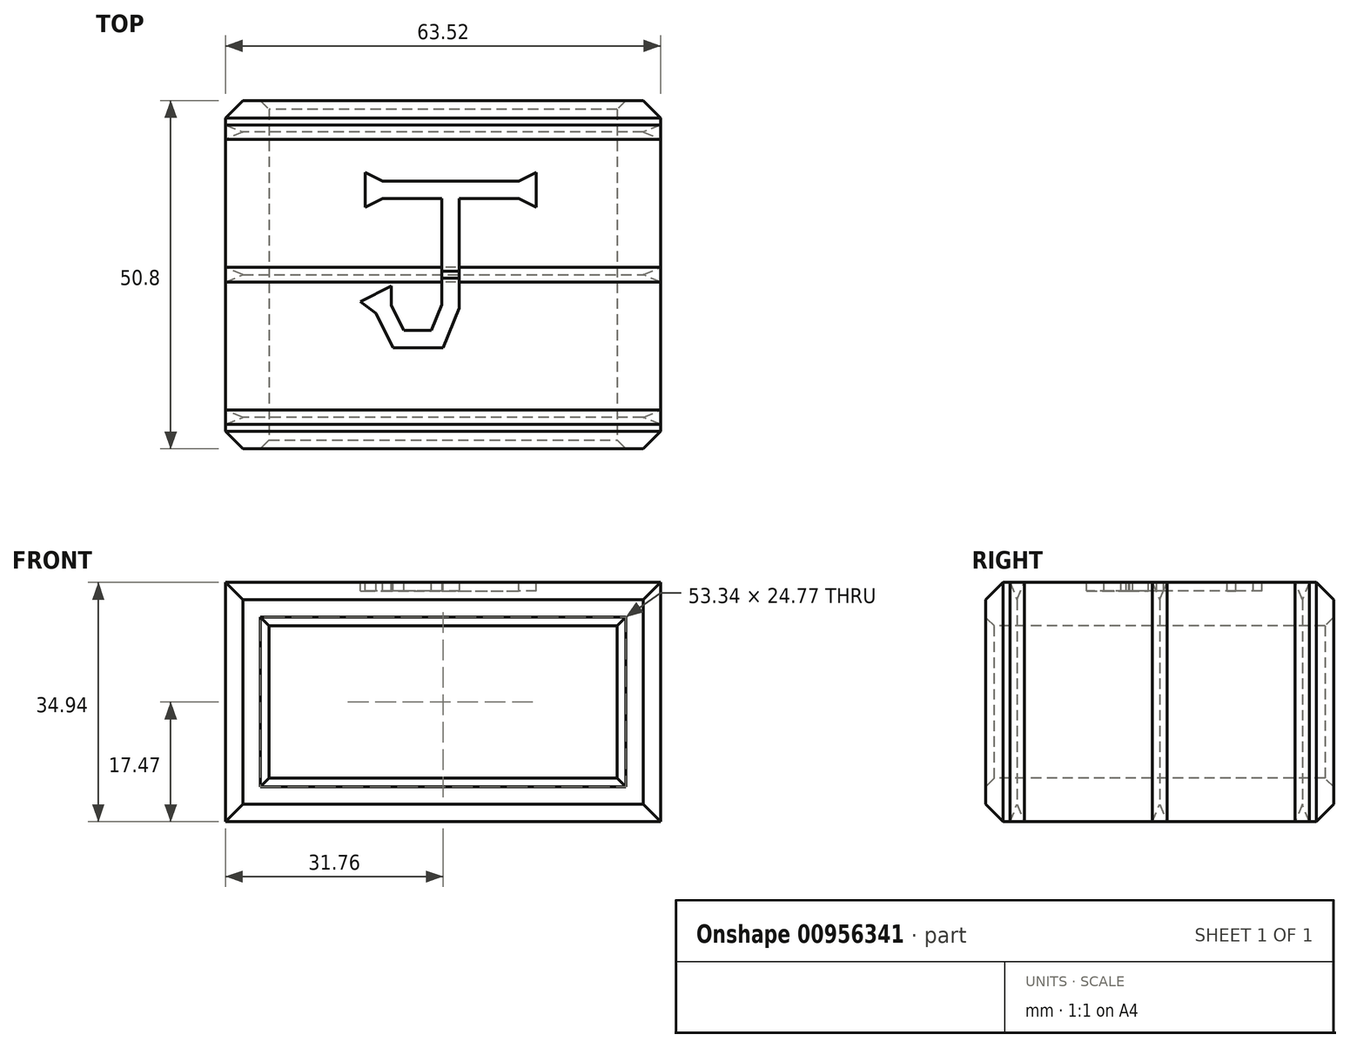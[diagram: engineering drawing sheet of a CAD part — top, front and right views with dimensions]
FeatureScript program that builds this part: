
annotation { "Feature Type Name" : "Feature", "Feature Type Description" : "" }
export const myFeature = defineFeature(function(context is Context, id is Id, definition is map)
    precondition{}
    {
        {
            var Q0;
            Q0=qCreatedBy(makeId("Front.planeOp"),FACE);
            var sketch = newSketch(context, id + "F0", { "sketchPlane" : qUnion([Q0])});
            skLineSegment(sketch, "E0.bottom", {"start": v(25.4, 11.11) * mm, "end": v(-25.4, 11.11) * mm});
            skLineSegment(sketch, "E0.top", {"start": v(25.4, -11.11) * mm, "end": v(-25.4, -11.11) * mm});
            skLineSegment(sketch, "E0.left", {"start": v(25.4, 11.11) * mm, "end": v(25.4, -11.11) * mm});
            skLineSegment(sketch, "E0.right", {"start": v(-25.4, 11.11) * mm, "end": v(-25.4, -11.11) * mm});
            skPoint(sketch, "E0.middle", {"position": v(0, 0) * mm});
            skLineSegment(sketch, "E1.0", {"start": v(30.48, 16.2) * mm, "end": v(-30.48, 16.2) * mm});
            skLineSegment(sketch, "E1.1", {"start": v(30.48, 16.2) * mm, "end": v(30.48, -16.2) * mm});
            skLineSegment(sketch, "E1.2", {"start": v(30.48, -16.2) * mm, "end": v(-30.48, -16.2) * mm});
            skLineSegment(sketch, "E1.3", {"start": v(-30.48, 16.2) * mm, "end": v(-30.48, -16.2) * mm});
            skSolve(sketch);
        }
        {
            var Q0;
            Q0=qCreatedBy(makeId("Right.planeOp"),FACE);
            var sketch = newSketch(context, id + "F1", { "sketchPlane" : qUnion([Q0])});
            skLineSegment(sketch, "E2", {"start": v(50.8, 11.11) * mm, "end": v(50.8, 14.92) * mm});
            skLineSegment(sketch, "E3", {"start": v(50.8, 14.92) * mm, "end": v(48.25, 17.47) * mm});
            skLineSegment(sketch, "E4", {"start": v(48.25, 17.47) * mm, "end": v(47.27, 17.47) * mm});
            skLineSegment(sketch, "E5", {"start": v(47.27, 17.47) * mm, "end": v(46.21, 14.92) * mm});
            skLineSegment(sketch, "E6", {"start": v(46.21, 14.92) * mm, "end": v(45.16, 17.47) * mm});
            skLineSegment(sketch, "E7", {"start": v(45.16, 17.47) * mm, "end": v(26.46, 17.47) * mm});
            skLineSegment(sketch, "E8", {"start": v(26.46, 17.47) * mm, "end": v(25.4, 14.92) * mm});
            skLineSegment(sketch, "E9", {"start": v(25.4, 14.92) * mm, "end": v(24.34, 17.47) * mm});
            skLineSegment(sketch, "E10", {"start": v(24.34, 17.47) * mm, "end": v(5.64, 17.47) * mm});
            skLineSegment(sketch, "E11", {"start": v(5.64, 17.47) * mm, "end": v(4.59, 14.92) * mm});
            skLineSegment(sketch, "E12", {"start": v(4.59, 14.92) * mm, "end": v(3.53, 17.47) * mm});
            skLineSegment(sketch, "E13", {"start": v(3.53, 17.47) * mm, "end": v(2.55, 17.47) * mm});
            skLineSegment(sketch, "E14", {"start": v(2.55, 17.47) * mm, "end": v(0, 14.92) * mm});
            skLineSegment(sketch, "E15", {"start": v(0, 14.92) * mm, "end": v(0, 11.11) * mm});
            skLineSegment(sketch, "E16", {"start": v(46.21, 14.92) * mm, "end": v(46.21, 38.18) * mm, "construction": true});
            skLineSegment(sketch, "E17", {"start": v(25.4, 14.92) * mm, "end": v(25.4, 36.3) * mm, "construction": true});
            skLineSegment(sketch, "E18", {"start": v(25.4, 36.3) * mm, "end": v(41.2, 36.3) * mm, "construction": true});
            skLineSegment(sketch, "E19", {"start": v(4.59, 14.92) * mm, "end": v(4.59, 35.3) * mm, "construction": true});
            skLineSegment(sketch, "E20", {"start": v(0, 14.92) * mm, "end": v(0, 38.69) * mm, "construction": true});
            skLineSegment(sketch, "E21", {"start": v(50.8, 14.92) * mm, "end": v(50.8, 38.2) * mm, "construction": true});
            skLineSegment(sketch, "E22", {"start": v(50.8, 14.92) * mm, "end": v(0, 14.92) * mm, "construction": true});
            skLineSegment(sketch, "E23", {"start": v(0, 11.11) * mm, "end": v(50.8, 11.11) * mm});
            skPoint(sketch, "E24.start.orphan", {"position": v(0, -70.86) * mm});
            skSolve(sketch);
        }
        {
            var Q0;
            Q0=makeQuery(id+"F1.imprint","IMPRINT",FACE,{"disambiguationData":[TD([[makeQuery(id+"F1.imprint","IMPRINT",EDGE,{"derivedFrom":sQuery(id+"F1.wireOp",EDGE,"E2")}),1.0]])]});
            var sketch = newSketch(context, id + "F2", { "sketchPlane" : qUnion([Q0])});
            skLineSegment(sketch, "E25", {"start": v(47.27, 17.47) * mm, "end": v(45.16, 17.47) * mm});
            skLineSegment(sketch, "E26", {"start": v(45.16, 17.47) * mm, "end": v(46.21, 14.92) * mm});
            skLineSegment(sketch, "E27", {"start": v(46.21, 14.92) * mm, "end": v(47.27, 17.47) * mm});
            skLineSegment(sketch, "E28", {"start": v(26.46, 17.47) * mm, "end": v(24.34, 17.47) * mm});
            skLineSegment(sketch, "E29", {"start": v(24.34, 17.47) * mm, "end": v(25.4, 14.92) * mm});
            skLineSegment(sketch, "E30", {"start": v(25.4, 14.92) * mm, "end": v(26.46, 17.47) * mm});
            skLineSegment(sketch, "E31", {"start": v(5.64, 17.47) * mm, "end": v(4.59, 14.92) * mm});
            skLineSegment(sketch, "E32", {"start": v(4.59, 14.92) * mm, "end": v(3.53, 17.47) * mm});
            skLineSegment(sketch, "E33", {"start": v(3.53, 17.47) * mm, "end": v(5.64, 17.47) * mm});
            skSolve(sketch);
        }
        {
            var Q0;
            Q0=makeQuery(id+"F1.imprint","IMPRINT",FACE,{"disambiguationData":[TD([[makeQuery(id+"F1.imprint","IMPRINT",EDGE,{"derivedFrom":sQuery(id+"F1.wireOp",EDGE,"E2")}),1.0]])]});
            var Q1;
            Q1=sQuery(id+"F0.wireOp",EDGE,"E0.bottom");
            var Q2;
            Q2=sQuery(id+"F0.wireOp",EDGE,"E0.left");
            var Q3;
            Q3=sQuery(id+"F0.wireOp",EDGE,"E0.top");
            var Q4;
            Q4=sQuery(id+"F0.wireOp",EDGE,"E0.right");
            sweep(context, id + "F3", {"profiles" : qUnion([Q0]), "path" : qUnion([Q1, Q2, Q3, Q4])});
        }
        {
            var Q0;
            Q0 = qSketchRegion(id + "F2", true);
            var Q1;
            Q1=makeQuery(id+"F3.opSweep","SWEPT_EDGE",EDGE,{"disambiguationData":[OSD([sQuery(id+"F0.wireOp",EDGE,"E0.right"),sQuery(id+"F1.wireOp",EDGE,"E11"),sQuery(id+"F1.wireOp",EDGE,"E12")])]});
            var Q2;
            Q2=makeQuery(id+"F3.opSweep","SWEPT_EDGE",EDGE,{"disambiguationData":[OSD([sQuery(id+"F0.wireOp",EDGE,"E0.bottom"),sQuery(id+"F1.wireOp",EDGE,"E11"),sQuery(id+"F1.wireOp",EDGE,"E12")])]});
            var Q3;
            Q3=makeQuery(id+"F3.opSweep","SWEPT_EDGE",EDGE,{"disambiguationData":[OSD([sQuery(id+"F0.wireOp",EDGE,"E0.top"),sQuery(id+"F1.wireOp",EDGE,"E11"),sQuery(id+"F1.wireOp",EDGE,"E12")])]});
            var Q4;
            Q4=makeQuery(id+"F3.opSweep","SWEPT_EDGE",EDGE,{"disambiguationData":[OSD([sQuery(id+"F0.wireOp",EDGE,"E0.left"),sQuery(id+"F1.wireOp",EDGE,"E11"),sQuery(id+"F1.wireOp",EDGE,"E12")])]});
            sweep(context, id + "F4", {"profiles" : qUnion([Q0]), "path" : qUnion([Q1, Q2, Q3, Q4])});
        }
        {
            var Q0;
            Q0=makeQuery(id+"F3.opSweep","SWEPT_EDGE",EDGE,{"disambiguationData":[OSD([sQuery(id+"F0.wireOp",EDGE,"E0.top"),sQuery(id+"F1.wireOp",EDGE,"E15"),sQuery(id+"F1.wireOp",EDGE,"E23")])]});
            var Q1;
            Q1=makeQuery(id+"F3.opSweep","SWEPT_EDGE",EDGE,{"disambiguationData":[OSD([sQuery(id+"F0.wireOp",EDGE,"E0.right"),sQuery(id+"F1.wireOp",EDGE,"E15"),sQuery(id+"F1.wireOp",EDGE,"E23")])]});
            var Q2;
            Q2=makeQuery(id+"F3.opSweep","SWEPT_EDGE",EDGE,{"disambiguationData":[OSD([sQuery(id+"F0.wireOp",EDGE,"E0.bottom"),sQuery(id+"F1.wireOp",EDGE,"E15"),sQuery(id+"F1.wireOp",EDGE,"E23")])]});
            var Q3;
            Q3=makeQuery(id+"F3.opSweep","SWEPT_EDGE",EDGE,{"disambiguationData":[OSD([sQuery(id+"F0.wireOp",EDGE,"E0.left"),sQuery(id+"F1.wireOp",EDGE,"E15"),sQuery(id+"F1.wireOp",EDGE,"E23")])]});
            var Q4;
            Q4=makeQuery(id+"F3.opSweep","SWEPT_EDGE",EDGE,{"disambiguationData":[OSD([sQuery(id+"F0.wireOp",EDGE,"E0.top"),sQuery(id+"F1.wireOp",EDGE,"E2"),sQuery(id+"F1.wireOp",EDGE,"E23")])]});
            var Q5;
            Q5=makeQuery(id+"F3.opSweep","SWEPT_EDGE",EDGE,{"disambiguationData":[OSD([sQuery(id+"F0.wireOp",EDGE,"E0.left"),sQuery(id+"F1.wireOp",EDGE,"E2"),sQuery(id+"F1.wireOp",EDGE,"E23")])]});
            var Q6;
            Q6=makeQuery(id+"F3.opSweep","SWEPT_EDGE",EDGE,{"disambiguationData":[OSD([sQuery(id+"F0.wireOp",EDGE,"E0.bottom"),sQuery(id+"F1.wireOp",EDGE,"E2"),sQuery(id+"F1.wireOp",EDGE,"E23")])]});
            var Q7;
            Q7=makeQuery(id+"F3.opSweep","SWEPT_EDGE",EDGE,{"disambiguationData":[OSD([sQuery(id+"F0.wireOp",EDGE,"E0.right"),sQuery(id+"F1.wireOp",EDGE,"E2"),sQuery(id+"F1.wireOp",EDGE,"E23")])]});
            chamfer(context, id + "F5", {"entities" : qUnion([Q0, Q1, Q2, Q3, Q4, Q5, Q6, Q7]), "width" : 1.27 * mm, "tangentPropagation" : true});
        }
        {
            var Q0;
            Q0=makeQuery(id+"F3.opSweep","SWEPT_FACE",FACE,{"disambiguationData":[OSD([sQuery(id+"F0.wireOp",EDGE,"E0.bottom"),sQuery(id+"F1.wireOp",EDGE,"E10")])]});
            var sketch = newSketch(context, id + "F6", { "sketchPlane" : qUnion([Q0])});
            skLineSegment(sketch, "E34", {"start": v(-8.85, 39.03) * mm, "end": v(11.06, 39.03) * mm});
            skLineSegment(sketch, "E35", {"start": v(-8.85, 36.49) * mm, "end": v(-0.16, 36.49) * mm});
            skLineSegment(sketch, "E36", {"start": v(-0.16, 36.49) * mm, "end": v(-0.16, 21.02) * mm});
            skLineSegment(sketch, "E37", {"start": v(2.38, 36.49) * mm, "end": v(2.38, 20.52) * mm});
            skLineSegment(sketch, "E38", {"start": v(-0.16, 21.02) * mm, "end": v(-1.7, 17.3) * mm});
            skLineSegment(sketch, "E39", {"start": v(2.38, 20.52) * mm, "end": v(0, 14.76) * mm});
            skLineSegment(sketch, "E40", {"start": v(-1.7, 17.3) * mm, "end": v(-5.73, 17.3) * mm});
            skLineSegment(sketch, "E41", {"start": v(0, 14.76) * mm, "end": v(-7.3, 14.76) * mm});
            skLineSegment(sketch, "E42", {"start": v(-5.73, 17.3) * mm, "end": v(-7.54, 20.9) * mm});
            skLineSegment(sketch, "E43", {"start": v(-7.3, 14.76) * mm, "end": v(-9.8, 19.75) * mm});
            skLineSegment(sketch, "E44", {"start": v(-11.39, 40.3) * mm, "end": v(-11.39, 35.22) * mm});
            skLineSegment(sketch, "E45", {"start": v(13.6, 40.3) * mm, "end": v(13.6, 35.22) * mm});
            skLineSegment(sketch, "E46", {"start": v(-7.55, 23.73) * mm, "end": v(-12.08, 21.45) * mm});
            skLineSegment(sketch, "E47", {"start": v(-8.85, 39.03) * mm, "end": v(-8.85, 36.49) * mm});
            skLineSegment(sketch, "E48", {"start": v(11.06, 39.03) * mm, "end": v(11.06, 36.49) * mm});
            skLineSegment(sketch, "E49", {"start": v(-11.39, 35.22) * mm, "end": v(13.6, 35.22) * mm, "construction": true});
            skLineSegment(sketch, "E50", {"start": v(-11.39, 40.3) * mm, "end": v(13.6, 40.3) * mm, "construction": true});
            skLineSegment(sketch, "E51", {"start": v(-7.55, 23.73) * mm, "end": v(-5.47, 19.6) * mm, "construction": true});
            skLineSegment(sketch, "E52", {"start": v(-12.08, 21.45) * mm, "end": v(-7.55, 12.44) * mm, "construction": true});
            skLineSegment(sketch, "E53", {"start": v(-11.39, 35.22) * mm, "end": v(-8.85, 36.49) * mm});
            skLineSegment(sketch, "E54", {"start": v(-11.39, 40.3) * mm, "end": v(-8.85, 39.03) * mm});
            skLineSegment(sketch, "E55", {"start": v(13.6, 40.3) * mm, "end": v(11.06, 39.03) * mm});
            skLineSegment(sketch, "E56", {"start": v(13.6, 35.22) * mm, "end": v(11.06, 36.49) * mm});
            skLineSegment(sketch, "E57", {"start": v(-7.54, 20.9) * mm, "end": v(-7.55, 23.73) * mm});
            skLineSegment(sketch, "E58", {"start": v(-12.08, 21.45) * mm, "end": v(-9.8, 19.75) * mm});
            skLineSegment(sketch, "E59.trimOffspring", {"start": v(2.38, 36.49) * mm, "end": v(11.06, 36.49) * mm});
            skLineSegment(sketch, "E60", {"start": v(-9.8, 19.75) * mm, "end": v(-7.54, 20.9) * mm, "construction": true});
            skLineSegment(sketch, "E61", {"start": v(1.1, 39.03) * mm, "end": v(1.1, 36.49) * mm, "construction": true});
            skLineSegment(sketch, "E62", {"start": v(2.38, 36.49) * mm, "end": v(-0.16, 36.49) * mm, "construction": true});
            skPoint(sketch, "E63", {"position": v(1.1, 36.49) * mm});
            skSolve(sketch);
        }
        {
            var Q0;
            {var subQ0=sQuery(id+"F6.wireOp",EDGE,"E38");Q0=makeQuery(id+"F6.imprint","IMPRINT",FACE,{"disambiguationData":[TD([[makeQuery(id+"F6.imprint","IMPRINT",EDGE,{"derivedFrom":subQ0}),1.0]])]});}
            var Q1;
            Q1=makeQuery(id+"F6.imprint","IMPRINT",FACE,{"disambiguationData":[TD([[makeQuery(id+"F6.imprint","IMPRINT",EDGE,{"derivedFrom":sQuery(id+"F6.wireOp",EDGE,"E34")}),-1.0]])]});
            var Q2;
            Q2=makeQuery(id+"F6.imprint","IMPRINT",FACE,{"disambiguationData":[TD([[makeQuery(id+"F6.imprint","IMPRINT",EDGE,{"derivedFrom":sQuery(id+"F6.wireOp",EDGE,"E44")}),1.0]])]});
            var Q3;
            Q3=makeQuery(id+"F6.imprint","IMPRINT",FACE,{"disambiguationData":[TD([[makeQuery(id+"F6.imprint","IMPRINT",EDGE,{"derivedFrom":sQuery(id+"F6.wireOp",EDGE,"E45")}),-1.0]])]});
            extrude(context, id + "F7", {"entities" : qUnion([Q0, Q1, Q2, Q3]), "operationType" : NewBodyOperationType.REMOVE, "oppositeDirection" : true, "depth" : 1.27 * mm, "offsetDistance" : 25.4 * mm});
        }
        {
            var Q0;
            {var subQ0=sQuery(id+"F6.wireOp",EDGE,"E55");var subQ1=sQuery(id+"F6.wireOp",EDGE,"E45");var subQ2=sQuery(id+"F6.wireOp",EDGE,"E44");var subQ3=sQuery(id+"F6.wireOp",EDGE,"E54");var subQ4=sQuery(id+"F6.wireOp",EDGE,"E37");var subQ5=sQuery(id+"F6.wireOp",EDGE,"E34");var subQ6=sQuery(id+"F6.wireOp",EDGE,"E35");var subQ7=sQuery(id+"F6.wireOp",EDGE,"E53");var subQ8=sQuery(id+"F6.wireOp",EDGE,"E36");var subQ9=sQuery(id+"F6.wireOp",EDGE,"E56");var subQ10=sQuery(id+"F6.wireOp",EDGE,"E59.trimOffspring");Q0=makeQuery(id+"F7.boolean.opBoolean","COPY",FACE,{"disambiguationData":[TD([makeQuery(id+"F7.opExtrude","SWEPT_FACE",FACE,{"disambiguationData":[OSD([subQ5])]})])],"derivedFrom":makeQuery(id+"F7.opExtrude","CAP_FACE",FACE,{"disambiguationData":[OSD([subQ5,subQ6,subQ8,subQ4,sQuery(id+"F6.wireOp",EDGE,"E38"),sQuery(id+"F6.wireOp",EDGE,"E39"),sQuery(id+"F6.wireOp",EDGE,"E40"),sQuery(id+"F6.wireOp",EDGE,"E41"),sQuery(id+"F6.wireOp",EDGE,"E42"),sQuery(id+"F6.wireOp",EDGE,"E43"),subQ2,subQ1,sQuery(id+"F6.wireOp",EDGE,"E46"),subQ7,subQ3,subQ0,subQ9,sQuery(id+"F6.wireOp",EDGE,"E57"),sQuery(id+"F6.wireOp",EDGE,"E58"),subQ10])],"isStart":false})});}
            var Q1;
            {var subQ0=sQuery(id+"F6.wireOp",EDGE,"E46");var subQ1=sQuery(id+"F6.wireOp",EDGE,"E43");var subQ2=sQuery(id+"F6.wireOp",EDGE,"E42");var subQ3=sQuery(id+"F6.wireOp",EDGE,"E41");var subQ4=sQuery(id+"F6.wireOp",EDGE,"E39");var subQ5=sQuery(id+"F6.wireOp",EDGE,"E40");var subQ6=sQuery(id+"F6.wireOp",EDGE,"E38");var subQ7=sQuery(id+"F6.wireOp",EDGE,"E36");var subQ8=sQuery(id+"F6.wireOp",EDGE,"E37");var subQ9=sQuery(id+"F6.wireOp",EDGE,"E57");var subQ10=sQuery(id+"F6.wireOp",EDGE,"E58");Q1=makeQuery(id+"F7.boolean.opBoolean","COPY",FACE,{"disambiguationData":[TD([makeQuery(id+"F7.opExtrude","SWEPT_FACE",FACE,{"disambiguationData":[OSD([subQ6])]})])],"derivedFrom":makeQuery(id+"F7.opExtrude","CAP_FACE",FACE,{"disambiguationData":[OSD([sQuery(id+"F6.wireOp",EDGE,"E34"),sQuery(id+"F6.wireOp",EDGE,"E35"),subQ7,subQ8,subQ6,subQ4,subQ5,subQ3,subQ2,subQ1,sQuery(id+"F6.wireOp",EDGE,"E44"),sQuery(id+"F6.wireOp",EDGE,"E45"),subQ0,sQuery(id+"F6.wireOp",EDGE,"E53"),sQuery(id+"F6.wireOp",EDGE,"E54"),sQuery(id+"F6.wireOp",EDGE,"E55"),sQuery(id+"F6.wireOp",EDGE,"E56"),subQ9,subQ10,sQuery(id+"F6.wireOp",EDGE,"E59.trimOffspring")])],"isStart":false})});}
            var Q2;
            {var subQ0=sQuery(id+"F1.wireOp",EDGE,"E12");var subQ1=sQuery(id+"F1.wireOp",EDGE,"E11");var subQ2=sQuery(id+"F0.wireOp",EDGE,"E0.bottom");var subQ3=sQuery(id+"F6.wireOp",EDGE,"E36");var subQ4=sQuery(id+"F6.wireOp",EDGE,"E37");Q2=makeQuery(id+"F7.boolean.opBoolean","COPY",FACE,{"disambiguationData":[TD([makeQuery(id+"F4.opSweep","SWEPT_FACE",FACE,{"disambiguationData":[OSD([subQ2,subQ1,subQ0,sQuery(id+"F2.wireOp",EDGE,"E29")])]})])],"derivedFrom":makeQuery(id+"F7.opExtrude","CAP_FACE",FACE,{"disambiguationData":[OSD([sQuery(id+"F6.wireOp",EDGE,"E34"),sQuery(id+"F6.wireOp",EDGE,"E35"),subQ3,subQ4,sQuery(id+"F6.wireOp",EDGE,"E38"),sQuery(id+"F6.wireOp",EDGE,"E39"),sQuery(id+"F6.wireOp",EDGE,"E40"),sQuery(id+"F6.wireOp",EDGE,"E41"),sQuery(id+"F6.wireOp",EDGE,"E42"),sQuery(id+"F6.wireOp",EDGE,"E43"),sQuery(id+"F6.wireOp",EDGE,"E44"),sQuery(id+"F6.wireOp",EDGE,"E45"),sQuery(id+"F6.wireOp",EDGE,"E46"),sQuery(id+"F6.wireOp",EDGE,"E53"),sQuery(id+"F6.wireOp",EDGE,"E54"),sQuery(id+"F6.wireOp",EDGE,"E55"),sQuery(id+"F6.wireOp",EDGE,"E56"),sQuery(id+"F6.wireOp",EDGE,"E57"),sQuery(id+"F6.wireOp",EDGE,"E58"),sQuery(id+"F6.wireOp",EDGE,"E59.trimOffspring")])],"isStart":false})});}
            extrude(context, id + "F8", {"entities" : qUnion([Q0, Q1, Q2]), "depth" : 1.27 * mm, "offsetDistance" : 25.4 * mm});
        }
    });
